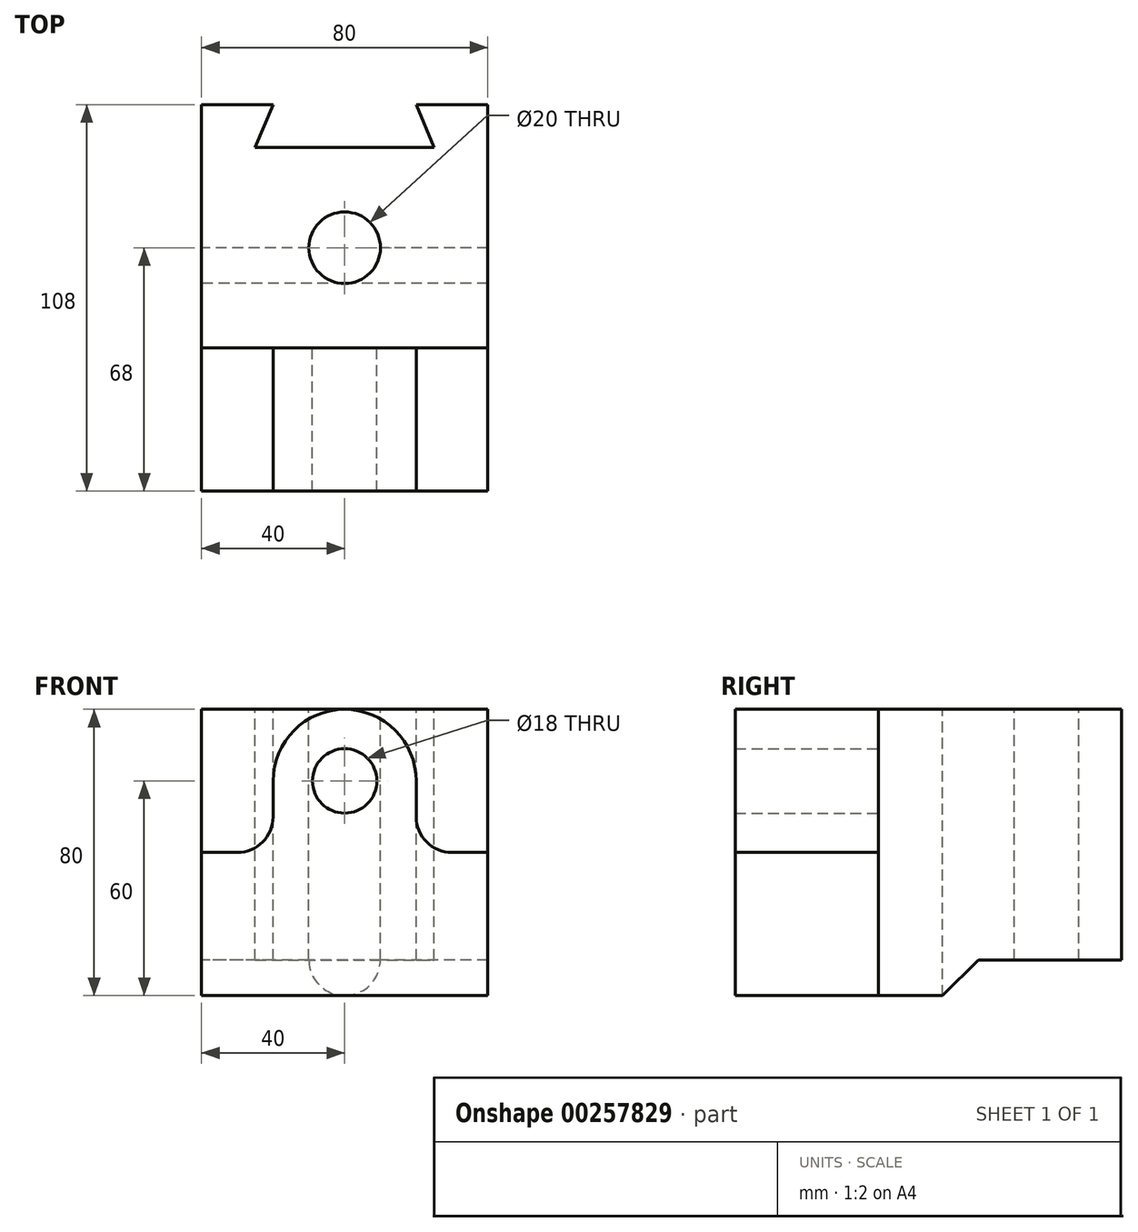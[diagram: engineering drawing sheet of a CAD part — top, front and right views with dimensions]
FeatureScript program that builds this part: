
annotation { "Feature Type Name" : "Feature", "Feature Type Description" : "" }
export const myFeature = defineFeature(function(context is Context, id is Id, definition is map)
    precondition{}
    {
        {
            var Q0;
            Q0=qCreatedBy(makeId("Front.planeOp"),FACE);
            var sketch = newSketch(context, id + "F0", { "sketchPlane" : qUnion([Q0])});
            skLineSegment(sketch, "E0", {"start": v(0, 0) * mm, "end": v(0, -31.6) * mm, "construction": true});
            skCircle(sketch, "E1", {"center": v(0, 0) * mm, "radius": 9 * mm});
            skLineSegment(sketch, "E2", {"start": v(0, 0) * mm, "end": v(0, 57.45) * mm, "construction": true});
            skCircle(sketch, "E3", {"center": v(0, 0) * mm, "radius": 20 * mm});
            skLineSegment(sketch, "E4", {"start": v(0, 20) * mm, "end": v(40, 20) * mm});
            skLineSegment(sketch, "E5", {"start": v(40, 20) * mm, "end": v(40, -60) * mm});
            skLineSegment(sketch, "E6", {"start": v(40, -60) * mm, "end": v(-40, -60) * mm});
            skLineSegment(sketch, "E7", {"start": v(-40, -60) * mm, "end": v(-40, 20) * mm});
            skLineSegment(sketch, "E8", {"start": v(-40, 20) * mm, "end": v(0, 20) * mm});
            skLineSegment(sketch, "E9", {"start": v(40, -10) * mm, "end": v(-11.6, -10) * mm, "construction": true});
            skArc(sketch, "E10", {"start": v(20, -10) * mm, "mid": v(22.93, -17.07) * mm, "end": v(30, -20) * mm});
            skLineSegment(sketch, "E11", {"start": v(20, -10) * mm, "end": v(20, 0) * mm});
            skArc(sketch, "E12.MirrorC", {"start": v(-20, -10) * mm, "mid": v(-22.93, -17.07) * mm, "end": v(-30, -20) * mm});
            skLineSegment(sketch, "E13.MirrorCS", {"start": v(-20, -10) * mm, "end": v(-20, 0) * mm});
            skLineSegment(sketch, "E14", {"start": v(40, -20) * mm, "end": v(30, -20) * mm});
            skLineSegment(sketch, "E15.MirrorCS", {"start": v(-40, -20) * mm, "end": v(-30, -20) * mm});
            skSolve(sketch);
        }
        {
            var Q0;
            Q0=makeQuery(id+"F0.imprint","IMPRINT",FACE,{"disambiguationData":[TD([[makeQuery(id+"F0.imprint","IMPRINT",EDGE,{"derivedFrom":sQuery(id+"F0.wireOp",EDGE,"E1")}),-1.0]])]});
            var Q1;
            {var subQ1=sQuery(id+"F0.wireOp",EDGE,"E6");Q1=makeQuery(id+"F0.imprint","IMPRINT",FACE,{"disambiguationData":[TD([[makeQuery(id+"F0.imprint","IMPRINT",EDGE,{"derivedFrom":subQ1}),-1.0]])]});}
            extrude(context, id + "F1", {"entities" : qUnion([Q0, Q1]), "depth" : 40 * mm});
        }
        {
            var Q0;
            Q0=makeQuery(id+"F1.opExtrude","SWEPT_FACE",FACE,{"disambiguationData":[OSD([sQuery(id+"F0.wireOp",EDGE,"E7")])]});
            var sketch = newSketch(context, id + "F2", { "sketchPlane" : qUnion([Q0])});
            skLineSegment(sketch, "E16", {"start": v(0, -60) * mm, "end": v(-18, -60) * mm});
            skLineSegment(sketch, "E17", {"start": v(-18, -50) * mm, "end": v(-91.95, -50) * mm, "construction": true});
            skLineSegment(sketch, "E18", {"start": v(-18, -50) * mm, "end": v(62.64, -50) * mm, "construction": true});
            skLineSegment(sketch, "E19", {"start": v(-18, -60) * mm, "end": v(-28, -50) * mm});
            skLineSegment(sketch, "E20", {"start": v(-18, -60) * mm, "end": v(-68, -60) * mm, "construction": true});
            skLineSegment(sketch, "E21", {"start": v(-68, -60) * mm, "end": v(-68, -43.24) * mm, "construction": true});
            skLineSegment(sketch, "E22", {"start": v(-28, -50) * mm, "end": v(-68, -50) * mm});
            skLineSegment(sketch, "E23", {"start": v(-68, -50) * mm, "end": v(-68, 20) * mm});
            skLineSegment(sketch, "E24", {"start": v(-68, 20) * mm, "end": v(0, 20) * mm});
            skLineSegment(sketch, "E25", {"start": v(0, 20) * mm, "end": v(0, -60) * mm});
            skSolve(sketch);
        }
        {
            var Q0;
            {var subQ0=sQuery(id+"F2.wireOp",EDGE,"E16");Q0=makeQuery(id+"F2.imprint","IMPRINT",FACE,{"disambiguationData":[TD([[makeQuery(id+"F2.imprint","IMPRINT",EDGE,{"derivedFrom":subQ0}),-1.0]])]});}
            extrude(context, id + "F3", {"entities" : qUnion([Q0]), "oppositeDirection" : true, "depth" : 80 * mm});
        }
        {
            var Q0;
            Q0=makeQuery(id+"F3.opExtrude","SWEPT_FACE",FACE,{"disambiguationData":[OSD([sQuery(id+"F2.wireOp",EDGE,"E24")])]});
            var sketch = newSketch(context, id + "F4", { "sketchPlane" : qUnion([Q0])});
            skLineSegment(sketch, "E26", {"start": v(-20, 68) * mm, "end": v(-20, 56) * mm, "construction": true});
            skLineSegment(sketch, "E27", {"start": v(-20, 68) * mm, "end": v(-25, 56) * mm});
            skLineSegment(sketch, "E28", {"start": v(-25, 56) * mm, "end": v(0, 56) * mm});
            skLineSegment(sketch, "E29", {"start": v(0, 56) * mm, "end": v(0, 23.22) * mm, "construction": true});
            skLineSegment(sketch, "E30.MirrorCS", {"start": v(25, 56) * mm, "end": v(0, 56) * mm});
            skLineSegment(sketch, "E31.MirrorCS", {"start": v(20, 68) * mm, "end": v(25, 56) * mm});
            skLineSegment(sketch, "E32", {"start": v(-20, 68) * mm, "end": v(20, 68) * mm});
            skSolve(sketch);
        }
        {
            var Q0;
            Q0=makeQuery(id+"F4.imprint","IMPRINT",FACE,{"disambiguationData":[TD([[makeQuery(id+"F4.imprint","IMPRINT",EDGE,{"derivedFrom":sQuery(id+"F4.wireOp",EDGE,"E27")}),1.0]])]});
            extrude(context, id + "F5", {"entities" : qUnion([Q0]), "oppositeDirection" : true, "depth" : 100 * mm});
        }
        {
            var Q0;
            Q0=makeQuery(id+"F5.opExtrude","SWEPT_BODY",BODY,{"disambiguationData":[OSD([sQuery(id+"F4.wireOp",EDGE,"E27"),sQuery(id+"F4.wireOp",EDGE,"E28"),sQuery(id+"F4.wireOp",EDGE,"E30.MirrorCS"),sQuery(id+"F4.wireOp",EDGE,"E31.MirrorCS"),sQuery(id+"F4.wireOp",EDGE,"E32")])]});
            var Q1;
            Q1=makeQuery(id+"F3.opExtrude","SWEPT_BODY",BODY,{"disambiguationData":[OSD([sQuery(id+"F2.wireOp",EDGE,"E16"),sQuery(id+"F2.wireOp",EDGE,"E19"),sQuery(id+"F2.wireOp",EDGE,"E22"),sQuery(id+"F2.wireOp",EDGE,"E23"),sQuery(id+"F2.wireOp",EDGE,"E24"),sQuery(id+"F2.wireOp",EDGE,"E25")])]});
            booleanBodies(context, id + "F6", {"operationType" : BooleanOperationType.SUBTRACTION, "tools" : qUnion([Q0]), "targets" : qUnion([Q1])});
        }
        {
            var Q0;
            Q0=makeQuery(id+"F3.opExtrude","SWEPT_FACE",FACE,{"disambiguationData":[OSD([sQuery(id+"F2.wireOp",EDGE,"E24")])]});
            var sketch = newSketch(context, id + "F7", { "sketchPlane" : qUnion([Q0])});
            skLineSegment(sketch, "E33", {"start": v(0, 0) * mm, "end": v(0, 56) * mm, "construction": true});
            skCircle(sketch, "E34", {"center": v(0, 28) * mm, "radius": 10 * mm});
            skSolve(sketch);
        }
        {
            var Q0;
            Q0=makeQuery(id+"F7.imprint","IMPRINT",FACE,{"disambiguationData":[TD([[makeQuery(id+"F7.imprint","IMPRINT",EDGE,{"derivedFrom":sQuery(id+"F7.wireOp",EDGE,"E34")}),1.0]])]});
            extrude(context, id + "F8", {"entities" : qUnion([Q0]), "oppositeDirection" : true, "depth" : 100 * mm});
        }
        {
            var Q0;
            Q0=makeQuery(id+"F8.opExtrude","SWEPT_BODY",BODY,{"disambiguationData":[OSD([sQuery(id+"F7.wireOp",EDGE,"E34")])]});
            var Q1;
            Q1=makeQuery(id+"F3.opExtrude","SWEPT_BODY",BODY,{"disambiguationData":[OSD([sQuery(id+"F2.wireOp",EDGE,"E16"),sQuery(id+"F2.wireOp",EDGE,"E19"),sQuery(id+"F2.wireOp",EDGE,"E22"),sQuery(id+"F2.wireOp",EDGE,"E23"),sQuery(id+"F2.wireOp",EDGE,"E24"),sQuery(id+"F2.wireOp",EDGE,"E25")])]});
            booleanBodies(context, id + "F9", {"operationType" : BooleanOperationType.SUBTRACTION, "tools" : qUnion([Q0]), "targets" : qUnion([Q1])});
        }
    });
